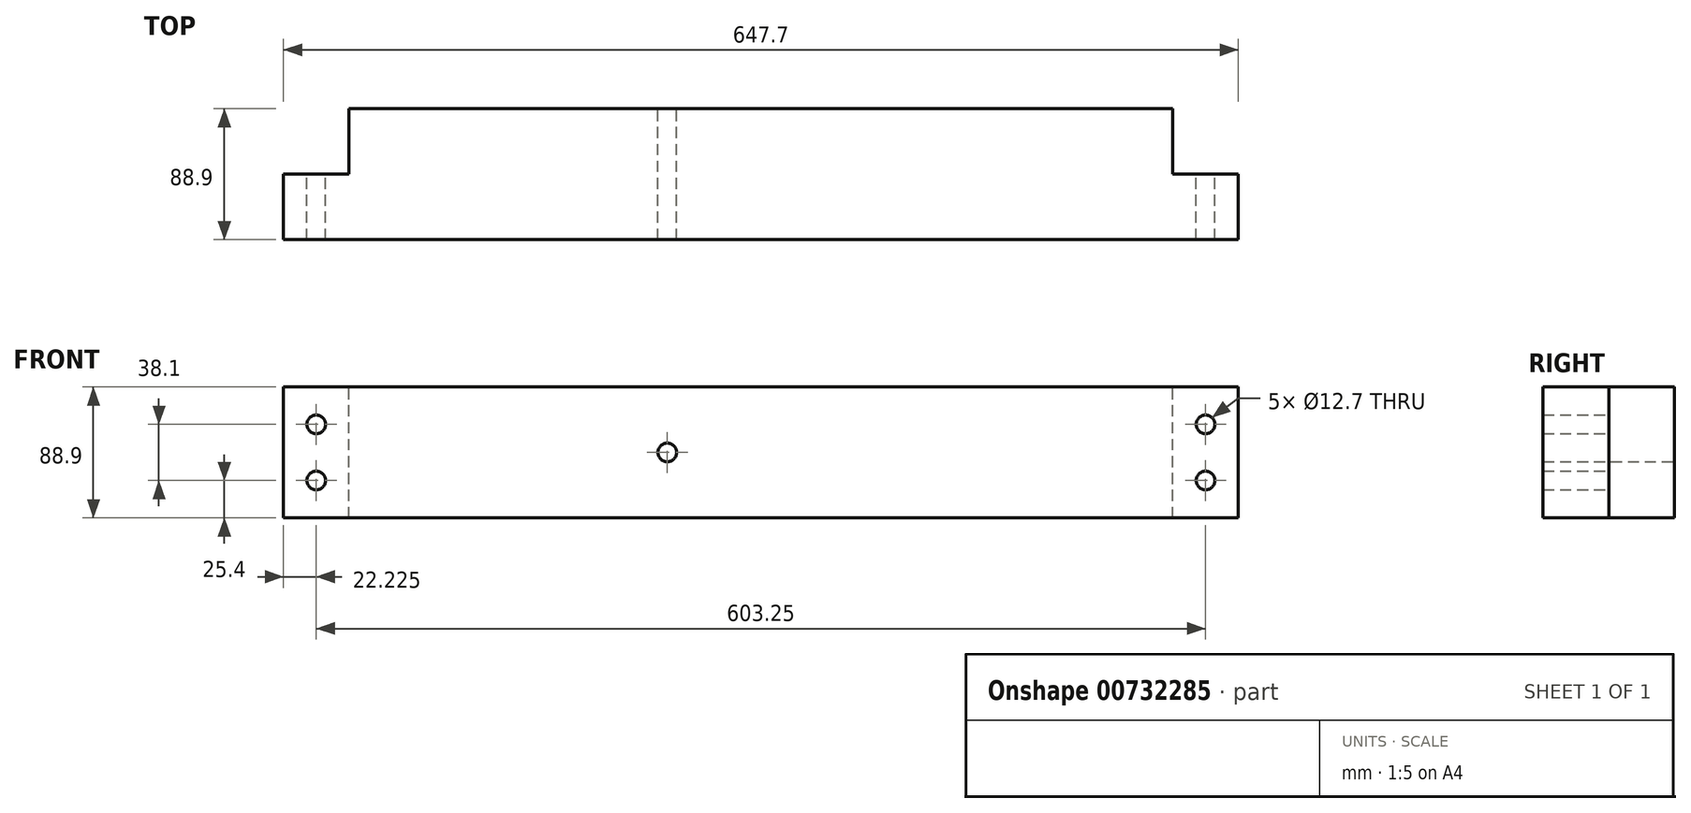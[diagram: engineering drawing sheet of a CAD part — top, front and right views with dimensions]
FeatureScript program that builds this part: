
annotation { "Feature Type Name" : "Feature", "Feature Type Description" : "" }
export const myFeature = defineFeature(function(context is Context, id is Id, definition is map)
    precondition{}
    {
        {
            var Q0;
            Q0=qCreatedBy(makeId("Front.planeOp"),FACE);
            var sketch = newSketch(context, id + "F0", { "sketchPlane" : qUnion([Q0])});
            skLineSegment(sketch, "E0.bottom", {"start": v(323.85, 44.45) * mm, "end": v(-323.85, 44.45) * mm});
            skLineSegment(sketch, "E0.top", {"start": v(323.85, -44.45) * mm, "end": v(-323.85, -44.45) * mm});
            skLineSegment(sketch, "E0.left", {"start": v(323.85, 44.45) * mm, "end": v(323.85, -44.45) * mm});
            skLineSegment(sketch, "E0.right", {"start": v(-323.85, 44.45) * mm, "end": v(-323.85, -44.45) * mm});
            skPoint(sketch, "E0.middle", {"position": v(0, 0) * mm});
            skLineSegment(sketch, "E1", {"start": v(-323.85, 0) * mm, "end": v(323.85, 0) * mm, "construction": true});
            skLineSegment(sketch, "E2", {"start": v(279.4, 44.45) * mm, "end": v(279.4, -44.45) * mm, "construction": true});
            skLineSegment(sketch, "E3", {"start": v(-279.4, 44.45) * mm, "end": v(-279.4, -44.45) * mm, "construction": true});
            skLineSegment(sketch, "E4", {"start": v(-301.63, -44.45) * mm, "end": v(-301.63, 44.45) * mm, "construction": true});
            skLineSegment(sketch, "E5", {"start": v(301.62, 44.45) * mm, "end": v(301.62, -44.45) * mm, "construction": true});
            skLineSegment(sketch, "E6", {"start": v(-323.85, 19.05) * mm, "end": v(323.85, 19.05) * mm, "construction": true});
            skLineSegment(sketch, "E7", {"start": v(323.85, -19.05) * mm, "end": v(-323.85, -19.05) * mm, "construction": true});
            skCircle(sketch, "E8", {"center": v(-301.63, 19.05) * mm, "radius": 6.35 * mm});
            skCircle(sketch, "E9", {"center": v(-301.63, -19.05) * mm, "radius": 6.35 * mm});
            skCircle(sketch, "E10", {"center": v(301.62, -19.05) * mm, "radius": 6.35 * mm});
            skCircle(sketch, "E11", {"center": v(301.62, 19.05) * mm, "radius": 6.35 * mm});
            skLineSegment(sketch, "E12", {"start": v(-63.5, 44.45) * mm, "end": v(-63.5, -44.45) * mm, "construction": true});
            skCircle(sketch, "E13", {"center": v(-63.5, 0) * mm, "radius": 6.35 * mm});
            skSolve(sketch);
        }
        {
            var Q0;
            Q0=makeQuery(id+"F0.imprint","IMPRINT",FACE,{"disambiguationData":[TD([[makeQuery(id+"F0.imprint","IMPRINT",EDGE,{"derivedFrom":sQuery(id+"F0.wireOp",EDGE,"E0.bottom")}),1.0]])]});
            extrude(context, id + "F1", {"entities" : qUnion([Q0]), "depth" : 88.9 * mm, "offsetDistance" : 25.4 * mm});
        }
        {
            var Q0;
            Q0=makeQuery(id+"F1.opExtrude","SWEPT_FACE",FACE,{"disambiguationData":[OSD([sQuery(id+"F0.wireOp",EDGE,"E0.bottom")])]});
            var sketch = newSketch(context, id + "F2", { "sketchPlane" : qUnion([Q0])});
            skLineSegment(sketch, "E14", {"start": v(-323.85, -44.45) * mm, "end": v(323.85, -44.45) * mm, "construction": true});
            skLineSegment(sketch, "E15", {"start": v(-279.4, 0) * mm, "end": v(-279.4, -44.45) * mm, "construction": true});
            skLineSegment(sketch, "E16", {"start": v(279.4, 0) * mm, "end": v(279.4, -44.45) * mm, "construction": true});
            skLineSegment(sketch, "E17.bottom", {"start": v(-323.85, 0) * mm, "end": v(-279.4, 0) * mm});
            skLineSegment(sketch, "E17.top", {"start": v(-323.85, -44.45) * mm, "end": v(-279.4, -44.45) * mm});
            skLineSegment(sketch, "E17.left", {"start": v(-323.85, 0) * mm, "end": v(-323.85, -44.45) * mm});
            skLineSegment(sketch, "E17.right", {"start": v(-279.4, 0) * mm, "end": v(-279.4, -44.45) * mm});
            skLineSegment(sketch, "E18.bottom", {"start": v(279.4, 0) * mm, "end": v(323.85, 0) * mm});
            skLineSegment(sketch, "E18.top", {"start": v(279.4, -44.45) * mm, "end": v(323.85, -44.45) * mm});
            skLineSegment(sketch, "E18.left", {"start": v(279.4, 0) * mm, "end": v(279.4, -44.45) * mm});
            skLineSegment(sketch, "E18.right", {"start": v(323.85, 0) * mm, "end": v(323.85, -44.45) * mm});
            skSolve(sketch);
        }
        {
            var Q0;
            Q0=makeQuery(id+"F2.imprint","IMPRINT",FACE,{"disambiguationData":[TD([[makeQuery(id+"F2.imprint","IMPRINT",EDGE,{"derivedFrom":sQuery(id+"F2.wireOp",EDGE,"E17.bottom")}),1.0]])]});
            var Q1;
            Q1=makeQuery(id+"F2.imprint","IMPRINT",FACE,{"disambiguationData":[TD([[makeQuery(id+"F2.imprint","IMPRINT",EDGE,{"derivedFrom":sQuery(id+"F2.wireOp",EDGE,"E18.bottom")}),1.0]])]});
            extrude(context, id + "F3", {"entities" : qUnion([Q0, Q1]), "operationType" : NewBodyOperationType.REMOVE, "oppositeDirection" : true, "depth" : 101.6 * mm, "offsetDistance" : 25.4 * mm});
        }
    });
